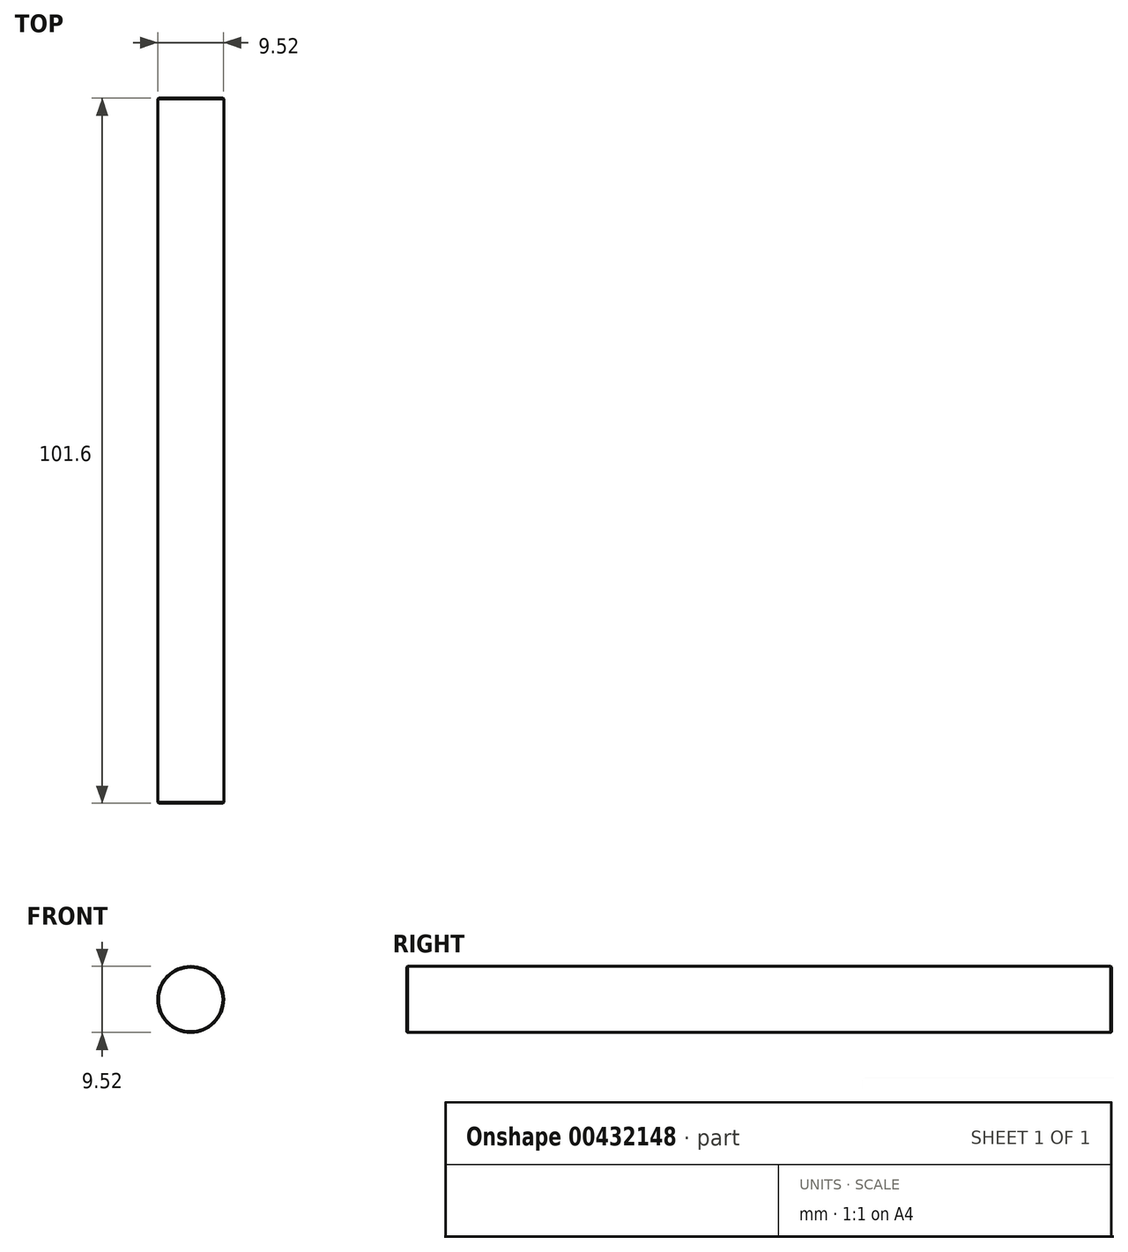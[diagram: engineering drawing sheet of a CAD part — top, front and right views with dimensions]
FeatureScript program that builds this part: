
annotation { "Feature Type Name" : "Feature", "Feature Type Description" : "" }
export const myFeature = defineFeature(function(context is Context, id is Id, definition is map)
    precondition{}
    {
        {
            var Q0;
            Q0=qCreatedBy(makeId("Front.planeOp"),FACE);
            var sketch = newSketch(context, id + "F0", { "sketchPlane" : qUnion([Q0])});
            skCircle(sketch, "E0", {"center": v(0, 0) * mm, "radius": 4.76 * mm});
            skSolve(sketch);
        }
        {
            var Q0;
            Q0=makeQuery(id+"F0.imprint","IMPRINT",FACE,{"disambiguationData":[TD([[makeQuery(id+"F0.imprint","IMPRINT",EDGE,{"derivedFrom":sQuery(id+"F0.wireOp",EDGE,"E0")}),1.0]])]});
            extrude(context, id + "F1", {"entities" : qUnion([Q0]), "depth" : 101.6 * mm, "symmetric" : true});
        }
        {
            var Q0;
            Q0=makeQuery(id+"F1.opExtrude","CAP_EDGE",EDGE,{"disambiguationData":[OSD([sQuery(id+"F0.wireOp",EDGE,"E0")])],"isStart":false});
            var Q1;
            Q1=makeQuery(id+"F1.opExtrude","CAP_EDGE",EDGE,{"disambiguationData":[OSD([sQuery(id+"F0.wireOp",EDGE,"E0")])],"isStart":true});
            chamfer(context, id + "F2", {"entities" : qUnion([Q0, Q1]), "width" : 0.13 * mm, "tangentPropagation" : true});
        }
    });
